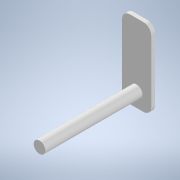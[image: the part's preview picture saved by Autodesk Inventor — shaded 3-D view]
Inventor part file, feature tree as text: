
AUTODESK INVENTOR PART (.ipt)
format: ipt  version: 2021 (Build 250183000, 183)  size: 113,152 bytes
history: native  units: mm
features: extrude x2, sketch x2, other x1, fillet x1
ambient origin geometry x8: Origin, YZ Plane, XZ Plane, XY Plane, X Axis, Y Axis, Z Axis, Center Point
bodies: Body1 (feature_tree)
feature tree (6):
  other  "Bryła1"
  extrude  "Wyciągnięcie proste1"  Depth=6.0mm
  extrude  "Wyciągnięcie proste2"  Depth=50.0mm TaperAngle=0.0deg
  fillet  "Zaokrąglenie1"  Radius=40.0mm
  sketch  "Szkic1"
  sketch  "Szkic2"
